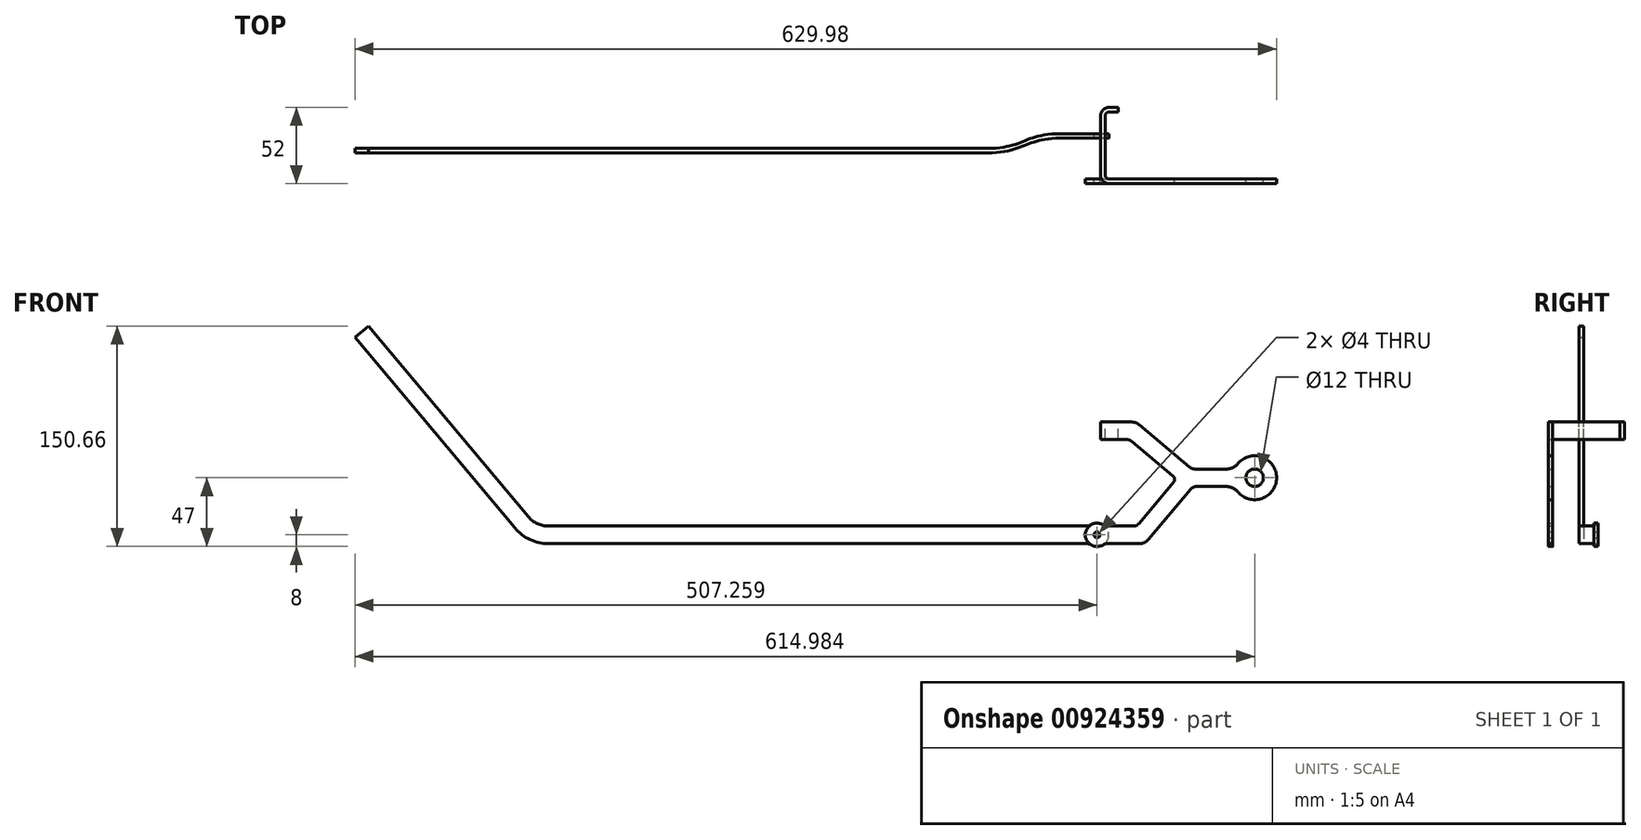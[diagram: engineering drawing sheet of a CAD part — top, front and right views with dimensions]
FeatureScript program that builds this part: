
annotation { "Feature Type Name" : "Feature", "Feature Type Description" : "" }
export const myFeature = defineFeature(function(context is Context, id is Id, definition is map)
    precondition{}
    {
        {
            var Q0;
            Q0=qCreatedBy(makeId("Front.planeOp"),FACE);
            var sketch = newSketch(context, id + "F0", { "sketchPlane" : qUnion([Q0])});
            skLineSegment(sketch, "E0", {"start": v(13.99, 0) * mm, "end": v(313.99, 0) * mm});
            skLineSegment(sketch, "E1", {"start": v(-9, 10.72) * mm, "end": v(-118.27, 140.94) * mm});
            skLineSegment(sketch, "E2", {"start": v(-23.81, 6) * mm, "end": v(-4.01, 6) * mm, "construction": true});
            skPoint(sketch, "E3.visualSharp", {"position": v(0, 0) * mm});
            skArc(sketch, "E3.filletArc", {"start": v(-9, 10.72) * mm, "mid": v(1.31, 2.81) * mm, "end": v(13.99, 0) * mm});
            skLineSegment(sketch, "E4.0", {"start": v(13.99, 12) * mm, "end": v(313.99, 12) * mm});
            skArc(sketch, "E4.1", {"start": v(0.2, 18.43) * mm, "mid": v(6.38, 13.69) * mm, "end": v(13.99, 12) * mm});
            skLineSegment(sketch, "E4.2", {"start": v(0.2, 18.43) * mm, "end": v(-109.07, 148.66) * mm});
            skLineSegment(sketch, "E5", {"start": v(-109.07, 148.66) * mm, "end": v(-118.27, 140.94) * mm});
            skLineSegment(sketch, "E6", {"start": v(313.99, 12) * mm, "end": v(313.99, 0) * mm});
            skSolve(sketch);
        }
        {
            var Q0;
            Q0=makeQuery(id+"F0.imprint","IMPRINT",FACE,{"disambiguationData":[TD([[makeQuery(id+"F0.imprint","IMPRINT",EDGE,{"derivedFrom":sQuery(id+"F0.wireOp",EDGE,"E0")}),1.0]])]});
            extrude(context, id + "F1", {"entities" : qUnion([Q0]), "depth" : 3 * mm, "offsetDistance" : 25 * mm});
        }
        {
            var Q0;
            Q0=qCreatedBy(makeId("Top.planeOp"),FACE);
            var sketch = newSketch(context, id + "F2", { "sketchPlane" : qUnion([Q0])});
            skLineSegment(sketch, "E7.0", {"start": v(13.99, 0) * mm, "end": v(313.99, 0) * mm});
            skSolve(sketch);
        }
        {
            var Q0;
            Q0=makeQuery(id+"F1.opExtrude","CAP_FACE",FACE,{"disambiguationData":[OSD([sQuery(id+"F0.wireOp",EDGE,"E0"),sQuery(id+"F0.wireOp",EDGE,"E1"),sQuery(id+"F0.wireOp",EDGE,"E3.filletArc"),sQuery(id+"F0.wireOp",EDGE,"E4.0"),sQuery(id+"F0.wireOp",EDGE,"E4.1"),sQuery(id+"F0.wireOp",EDGE,"E4.2"),sQuery(id+"F0.wireOp",EDGE,"E5"),sQuery(id+"F0.wireOp",EDGE,"E6")])],"isStart":true});
            cPlane(context, id + "F3", {"entities" : qUnion([Q0]), "cplaneType" : CPlaneType.OFFSET, "offset" : 25 * mm, "width" : 150 * mm, "height" : 150 * mm});
        }
        {
            var Q0;
            Q0=makeQuery(id+"F1.opExtrude","SWEPT_FACE",FACE,{"disambiguationData":[OSD([sQuery(id+"F0.wireOp",EDGE,"E0")])]});
            var sketch = newSketch(context, id + "F4", { "sketchPlane" : qUnion([Q0])});
            skPoint(sketch, "E8.0", {"position": v(313.99, 0) * mm});
            skFitSpline(sketch, "E9", {"points": [v(313.99, 0) * mm, v(363.99, -10) * mm], "startDerivative": vector(75, 0) * mm, "endDerivative": vector(75, 0) * mm});
            skLineSegment(sketch, "E10", {"start": v(363.99, -10) * mm, "end": v(388.99, -10) * mm});
            skLineSegment(sketch, "E11", {"start": v(363.99, -10) * mm, "end": v(241.15, -10) * mm, "construction": true});
            skSolve(sketch);
        }
        {
            var Q0;
            Q0=makeQuery(id+"F1.opExtrude","SWEPT_FACE",FACE,{"disambiguationData":[OSD([sQuery(id+"F0.wireOp",EDGE,"E6")])]});
            var Q1;
            Q1=sQuery(id+"F4.wireOp",EDGE,"E9");
            var Q2;
            Q2=sQuery(id+"F4.wireOp",EDGE,"E10");
            sweep(context, id + "F5", {"operationType" : NewBodyOperationType.ADD, "profiles" : qUnion([Q0]), "path" : qUnion([Q1, Q2])});
        }
        {
            var Q0;
            {var subQ0=sQuery(id+"F4.wireOp",EDGE,"E10");var subQ1=sQuery(id+"F0.wireOp",EDGE,"E6");Q0=makeQuery(id+"F5.opSweep","SWEPT_FACE",FACE,{"disambiguationData":[OSD([subQ1,subQ0]),TDD([makeQuery(id+"F1.opExtrude","CAP_EDGE",EDGE,{"disambiguationData":[OSD([subQ1])],"isStart":true}),subQ0])]});}
            var sketch = newSketch(context, id + "F6", { "sketchPlane" : qUnion([Q0])});
            skCircle(sketch, "E12", {"center": v(-388.99, 6) * mm, "radius": 6 * mm});
            skCircle(sketch, "E13", {"center": v(-388.99, 6) * mm, "radius": 2 * mm});
            skCircle(sketch, "E14", {"center": v(-388.99, 6) * mm, "radius": 8 * mm});
            skSolve(sketch);
        }
        {
            var Q0;
            {var subQ2=sQuery(id+"F0.wireOp",EDGE,"E6");var subQ4=sQuery(id+"F4.wireOp",EDGE,"E10");var subQ5=sQuery(id+"F0.wireOp",EDGE,"E0");var subQ6=makeQuery(id+"F5.opSweep","SWEPT_EDGE",EDGE,{"disambiguationData":[OSD([subQ5,subQ2,subQ4]),TDD([makeQuery(id+"F1.opExtrude","CAP_VERTEX",VERTEX,{"disambiguationData":[OSD([subQ5,subQ2])],"isStart":true}),subQ4])]});var subQ11=sQuery(id+"F6.wireOp",EDGE,"E14");var subQ13=makeQuery(id+"F6.imprint","INTERSECT",VERTEX,{"derivedFrom":[subQ6,subQ11]});Q0=makeQuery(id+"F6.imprint","IMPRINT",FACE,{"disambiguationData":[TD([[makeQuery(id+"F6.imprint","IMPRINT",EDGE,{"disambiguationData":[TD([[subQ13,1.0]])],"derivedFrom":subQ11}),1.0]])]});}
            var Q1;
            {var subQ1=sQuery(id+"F4.wireOp",VERTEX,"E10.end");var subQ2=sQuery(id+"F0.wireOp",EDGE,"E6");var subQ3=makeQuery(id+"F5.opSweep","CAP_EDGE",EDGE,{"disambiguationData":[OSD([subQ2,subQ1]),TDD([makeQuery(id+"F1.opExtrude","CAP_EDGE",EDGE,{"disambiguationData":[OSD([subQ2])],"isStart":true}),subQ1])],"isStart":false});var subQ9=sQuery(id+"F6.wireOp",EDGE,"E13");var subQ10=makeQuery(id+"F6.imprint","INTERSECT",VERTEX,{"disambiguationData":[OD(0.0)],"derivedFrom":[subQ3,subQ9]});Q1=makeQuery(id+"F6.imprint","IMPRINT",FACE,{"disambiguationData":[TD([[makeQuery(id+"F6.imprint","IMPRINT",EDGE,{"disambiguationData":[TD([[subQ10,1.0]])],"derivedFrom":subQ9}),-1.0]])]});}
            var Q2;
            {var subQ1=sQuery(id+"F4.wireOp",VERTEX,"E10.end");var subQ2=sQuery(id+"F0.wireOp",EDGE,"E6");var subQ3=makeQuery(id+"F5.opSweep","CAP_EDGE",EDGE,{"disambiguationData":[OSD([subQ2,subQ1]),TDD([makeQuery(id+"F1.opExtrude","CAP_EDGE",EDGE,{"disambiguationData":[OSD([subQ2])],"isStart":true}),subQ1])],"isStart":false});var subQ9=sQuery(id+"F6.wireOp",EDGE,"E13");var subQ10=makeQuery(id+"F6.imprint","INTERSECT",VERTEX,{"disambiguationData":[OD(0.0)],"derivedFrom":[subQ3,subQ9]});Q2=makeQuery(id+"F6.imprint","IMPRINT",FACE,{"disambiguationData":[TD([[makeQuery(id+"F6.imprint","IMPRINT",EDGE,{"disambiguationData":[TD([[subQ10,-1.0]])],"derivedFrom":subQ9}),-1.0]])]});}
            var Q3;
            {var subQ2=sQuery(id+"F0.wireOp",EDGE,"E6");var subQ4=sQuery(id+"F4.wireOp",EDGE,"E10");var subQ5=sQuery(id+"F0.wireOp",EDGE,"E0");var subQ6=makeQuery(id+"F5.opSweep","SWEPT_EDGE",EDGE,{"disambiguationData":[OSD([subQ5,subQ2,subQ4]),TDD([makeQuery(id+"F1.opExtrude","CAP_VERTEX",VERTEX,{"disambiguationData":[OSD([subQ5,subQ2])],"isStart":true}),subQ4])]});var subQ11=sQuery(id+"F6.wireOp",EDGE,"E14");var subQ12=makeQuery(id+"F6.imprint","INTERSECT",VERTEX,{"derivedFrom":[subQ6,subQ11]});Q3=makeQuery(id+"F6.imprint","IMPRINT",FACE,{"disambiguationData":[TD([[makeQuery(id+"F6.imprint","IMPRINT",EDGE,{"disambiguationData":[TD([[subQ12,-1.0]])],"derivedFrom":subQ11}),1.0]])]});}
            var Q4;
            {var subQ0=sQuery(id+"F6.wireOp",EDGE,"E13");var subQ1=sQuery(id+"F4.wireOp",VERTEX,"E10.end");var subQ2=sQuery(id+"F0.wireOp",EDGE,"E6");var subQ3=makeQuery(id+"F5.opSweep","CAP_EDGE",EDGE,{"disambiguationData":[OSD([subQ2,subQ1]),TDD([makeQuery(id+"F1.opExtrude","CAP_EDGE",EDGE,{"disambiguationData":[OSD([subQ2])],"isStart":true}),subQ1])],"isStart":false});var subQ4=makeQuery(id+"F6.imprint","INTERSECT",VERTEX,{"disambiguationData":[OD(0.0)],"derivedFrom":[subQ3,subQ0]});Q4=makeQuery(id+"F6.imprint","IMPRINT",FACE,{"disambiguationData":[TD([[makeQuery(id+"F6.imprint","IMPRINT",EDGE,{"disambiguationData":[TD([[subQ4,1.0]])],"derivedFrom":subQ0}),1.0]])]});}
            var Q5;
            {var subQ0=sQuery(id+"F6.wireOp",EDGE,"E13");var subQ1=sQuery(id+"F4.wireOp",VERTEX,"E10.end");var subQ2=sQuery(id+"F0.wireOp",EDGE,"E6");var subQ3=makeQuery(id+"F5.opSweep","CAP_EDGE",EDGE,{"disambiguationData":[OSD([subQ2,subQ1]),TDD([makeQuery(id+"F1.opExtrude","CAP_EDGE",EDGE,{"disambiguationData":[OSD([subQ2])],"isStart":true}),subQ1])],"isStart":false});var subQ4=makeQuery(id+"F6.imprint","INTERSECT",VERTEX,{"disambiguationData":[OD(0.0)],"derivedFrom":[subQ3,subQ0]});Q5=makeQuery(id+"F6.imprint","IMPRINT",FACE,{"disambiguationData":[TD([[makeQuery(id+"F6.imprint","IMPRINT",EDGE,{"disambiguationData":[TD([[subQ4,-1.0]])],"derivedFrom":subQ0}),1.0]])]});}
            extrude(context, id + "F7", {"entities" : qUnion([Q0, Q1, Q2, Q3, Q4, Q5]), "operationType" : NewBodyOperationType.ADD, "oppositeDirection" : true, "depth" : 3 * mm, "offsetDistance" : 25 * mm});
        }
        {
            var Q0;
            {var subQ0=sQuery(id+"F6.wireOp",EDGE,"E13");var subQ1=sQuery(id+"F4.wireOp",VERTEX,"E10.end");var subQ2=sQuery(id+"F0.wireOp",EDGE,"E6");var subQ3=makeQuery(id+"F5.opSweep","CAP_EDGE",EDGE,{"disambiguationData":[OSD([subQ2,subQ1]),TDD([makeQuery(id+"F1.opExtrude","CAP_EDGE",EDGE,{"disambiguationData":[OSD([subQ2])],"isStart":true}),subQ1])],"isStart":false});var subQ4=makeQuery(id+"F6.imprint","INTERSECT",VERTEX,{"disambiguationData":[OD(0.0)],"derivedFrom":[subQ3,subQ0]});Q0=makeQuery(id+"F6.imprint","IMPRINT",FACE,{"disambiguationData":[TD([[makeQuery(id+"F6.imprint","IMPRINT",EDGE,{"disambiguationData":[TD([[subQ4,1.0]])],"derivedFrom":subQ0}),1.0]])]});}
            var Q1;
            {var subQ0=sQuery(id+"F6.wireOp",EDGE,"E13");var subQ1=sQuery(id+"F4.wireOp",VERTEX,"E10.end");var subQ2=sQuery(id+"F0.wireOp",EDGE,"E6");var subQ3=makeQuery(id+"F5.opSweep","CAP_EDGE",EDGE,{"disambiguationData":[OSD([subQ2,subQ1]),TDD([makeQuery(id+"F1.opExtrude","CAP_EDGE",EDGE,{"disambiguationData":[OSD([subQ2])],"isStart":true}),subQ1])],"isStart":false});var subQ4=makeQuery(id+"F6.imprint","INTERSECT",VERTEX,{"disambiguationData":[OD(0.0)],"derivedFrom":[subQ3,subQ0]});Q1=makeQuery(id+"F6.imprint","IMPRINT",FACE,{"disambiguationData":[TD([[makeQuery(id+"F6.imprint","IMPRINT",EDGE,{"disambiguationData":[TD([[subQ4,-1.0]])],"derivedFrom":subQ0}),1.0]])]});}
            extrude(context, id + "F8", {"entities" : qUnion([Q0, Q1]), "operationType" : NewBodyOperationType.REMOVE, "oppositeDirection" : true, "depth" : 25 * mm, "offsetDistance" : 25 * mm});
        }
        {
            var Q0;
            {var subQ0=sQuery(id+"F0.wireOp",EDGE,"E4.0");Q0=makeQuery(id+"F7.boolean.opBoolean","INTERSECT",EDGE,{"derivedFrom":[makeQuery(id+"F5.boolean.opBoolean","MERGE",FACE,{"derivedFrom":[makeQuery(id+"F1.opExtrude","SWEPT_FACE",FACE,{"disambiguationData":[OSD([subQ0])]}),makeQuery(id+"F5.opSweep","SWEPT_FACE",FACE,{"disambiguationData":[OSD([subQ0,sQuery(id+"F0.wireOp",EDGE,"E6"),sQuery(id+"F4.wireOp",EDGE,"E9")])]})]}),makeQuery(id+"F7.opExtrude","SWEPT_FACE",FACE,{"disambiguationData":[OSD([sQuery(id+"F6.wireOp",EDGE,"E14")])]})]});}
            var Q1;
            {var subQ0=sQuery(id+"F0.wireOp",EDGE,"E0");Q1=makeQuery(id+"F7.boolean.opBoolean","INTERSECT",EDGE,{"derivedFrom":[makeQuery(id+"F5.boolean.opBoolean","MERGE",FACE,{"derivedFrom":[makeQuery(id+"F1.opExtrude","SWEPT_FACE",FACE,{"disambiguationData":[OSD([subQ0])]}),makeQuery(id+"F5.opSweep","SWEPT_FACE",FACE,{"disambiguationData":[OSD([subQ0,sQuery(id+"F0.wireOp",EDGE,"E6"),sQuery(id+"F4.wireOp",EDGE,"E9")])]})]}),makeQuery(id+"F7.opExtrude","SWEPT_FACE",FACE,{"disambiguationData":[OSD([sQuery(id+"F6.wireOp",EDGE,"E14")])]})]});}
            fillet(context, id + "F9", {"entities" : qUnion([Q0, Q1]), "radius" : 5 * mm, "tangentPropagation" : true, "allowEdgeOverflow" : false});
        }
        {
            var Q0;
            Q0=qCreatedBy(id+"F3.planeOp",FACE);
            var sketch = newSketch(context, id + "F10", { "sketchPlane" : qUnion([Q0])});
            skArc(sketch, "E15.0", {"start": v(-393.25, -0.77) * mm, "mid": v(-380.99, 6) * mm, "end": v(-393.25, 12.77) * mm});
            skPoint(sketch, "E16.orphan", {"position": v(-382.06, 12) * mm});
            skPoint(sketch, "E17.orphan", {"position": v(-388.99, 0) * mm});
            skPoint(sketch, "E18.orphan", {"position": v(-363.99, 12) * mm});
            skPoint(sketch, "E19.orphan", {"position": v(-363.99, 0) * mm});
            skLineSegment(sketch, "E20", {"start": v(-363.99, 0) * mm, "end": v(-363.99, -55) * mm, "construction": true});
            skLineSegment(sketch, "E21", {"start": v(-363.99, -55) * mm, "end": v(-590.7, -55) * mm, "construction": true});
            skCircle(sketch, "E22", {"center": v(-496.71, 45) * mm, "radius": 100 * mm});
            skArc(sketch, "E23", {"start": v(-485.19, 54.6) * mm, "mid": v(-511.71, 45) * mm, "end": v(-485.19, 35.4) * mm});
            skLineSegment(sketch, "E24", {"start": v(-388.99, 6) * mm, "end": v(-418.99, 6) * mm, "construction": true});
            skLineSegment(sketch, "E25", {"start": v(-418.99, 6) * mm, "end": v(-451.71, 45) * mm, "construction": true});
            skLineSegment(sketch, "E26", {"start": v(-451.71, 45) * mm, "end": v(-481.71, 45) * mm, "construction": true});
            skLineSegment(sketch, "E27.0", {"start": v(-455.72, 51) * mm, "end": v(-477.5, 51) * mm});
            skLineSegment(sketch, "E27.1", {"start": v(-417.7, 13.79) * mm, "end": v(-441.33, 41.96) * mm});
            skLineSegment(sketch, "E27.2", {"start": v(-395.92, 12) * mm, "end": v(-413.86, 12) * mm});
            skLineSegment(sketch, "E28.0", {"start": v(-456.84, 39) * mm, "end": v(-477.5, 39) * mm});
            skLineSegment(sketch, "E28.1", {"start": v(-424.18, 2.86) * mm, "end": v(-453.01, 37.21) * mm});
            skLineSegment(sketch, "E28.2", {"start": v(-395.92, 0) * mm, "end": v(-418.06, 0) * mm});
            skPoint(sketch, "E29.visualSharp", {"position": v(-482.97, 51) * mm});
            skArc(sketch, "E29.filletArc", {"start": v(-485.19, 54.6) * mm, "mid": v(-481.75, 51.94) * mm, "end": v(-477.5, 51) * mm});
            skPoint(sketch, "E30.visualSharp", {"position": v(-482.97, 39) * mm});
            skArc(sketch, "E30.filletArc", {"start": v(-477.5, 39) * mm, "mid": v(-481.75, 38.06) * mm, "end": v(-485.19, 35.4) * mm});
            skPoint(sketch, "E31.visualSharp", {"position": v(-454.51, 39) * mm});
            skArc(sketch, "E31.filletArc", {"start": v(-453.01, 37.21) * mm, "mid": v(-454.73, 38.53) * mm, "end": v(-456.84, 39) * mm});
            skPoint(sketch, "E32.visualSharp", {"position": v(-448.92, 51) * mm});
            skPoint(sketch, "E33.visualSharp", {"position": v(-416.2, 12) * mm});
            skArc(sketch, "E33.filletArc", {"start": v(-417.7, 13.79) * mm, "mid": v(-415.97, 12.47) * mm, "end": v(-413.86, 12) * mm});
            skPoint(sketch, "E34.visualSharp", {"position": v(-421.79, 0) * mm});
            skArc(sketch, "E34.filletArc", {"start": v(-424.18, 2.86) * mm, "mid": v(-421.44, 0.75) * mm, "end": v(-418.06, 0) * mm});
            skPoint(sketch, "E35.visualSharp", {"position": v(-394.28, 12) * mm});
            skArc(sketch, "E35.filletArc", {"start": v(-395.92, 12) * mm, "mid": v(-394.53, 12.2) * mm, "end": v(-393.25, 12.77) * mm});
            skPoint(sketch, "E36.visualSharp", {"position": v(-394.28, 0) * mm});
            skArc(sketch, "E36.filletArc", {"start": v(-393.25, -0.77) * mm, "mid": v(-394.53, -0.2) * mm, "end": v(-395.92, 0) * mm});
            skCircle(sketch, "E37", {"center": v(-496.71, 45) * mm, "radius": 6 * mm});
            skCircle(sketch, "E38.0", {"center": v(-388.99, 6) * mm, "radius": 2 * mm});
            skLineSegment(sketch, "E39", {"start": v(-451.71, 45) * mm, "end": v(-413.45, 77.1) * mm, "construction": true});
            skLineSegment(sketch, "E40.0", {"start": v(-452.5, 52.17) * mm, "end": v(-417.87, 81.23) * mm});
            skLineSegment(sketch, "E41.0", {"start": v(-440.96, 46.19) * mm, "end": v(-412.66, 69.94) * mm});
            skPoint(sketch, "E42.visualSharp", {"position": v(-453.9, 51) * mm});
            skArc(sketch, "E42.filletArc", {"start": v(-455.72, 51) * mm, "mid": v(-454, 51.3) * mm, "end": v(-452.5, 52.17) * mm});
            skPoint(sketch, "E43.visualSharp", {"position": v(-443.26, 44.26) * mm});
            skArc(sketch, "E43.filletArc", {"start": v(-440.96, 46.19) * mm, "mid": v(-442.02, 44.15) * mm, "end": v(-441.33, 41.96) * mm});
            skLineSegment(sketch, "E44", {"start": v(-413.45, 77.1) * mm, "end": v(-403.45, 77.1) * mm, "construction": true});
            skLineSegment(sketch, "E45.0", {"start": v(-409.45, 71.1) * mm, "end": v(-403.45, 71.1) * mm});
            skLineSegment(sketch, "E46.0", {"start": v(-412.72, 83.1) * mm, "end": v(-403.45, 83.1) * mm});
            skLineSegment(sketch, "E47", {"start": v(-403.45, 71.1) * mm, "end": v(-403.45, 83.1) * mm});
            skPoint(sketch, "E48.visualSharp", {"position": v(-415.64, 83.1) * mm});
            skArc(sketch, "E48.filletArc", {"start": v(-412.72, 83.1) * mm, "mid": v(-415.46, 82.62) * mm, "end": v(-417.87, 81.23) * mm});
            skPoint(sketch, "E49.visualSharp", {"position": v(-411.27, 71.1) * mm});
            skArc(sketch, "E49.filletArc", {"start": v(-409.45, 71.1) * mm, "mid": v(-411.16, 70.8) * mm, "end": v(-412.66, 69.94) * mm});
            skSolve(sketch);
        }
        {
            var Q0;
            Q0=makeQuery(id+"F10.imprint","IMPRINT",FACE,{"disambiguationData":[TD([[makeQuery(id+"F10.imprint","IMPRINT",EDGE,{"derivedFrom":sQuery(id+"F10.wireOp",EDGE,"E23")}),1.0]])]});
            var Q1;
            Q1=makeQuery(id+"F10.imprint","IMPRINT",FACE,{"disambiguationData":[TD([[makeQuery(id+"F10.imprint","IMPRINT",EDGE,{"derivedFrom":sQuery(id+"F10.wireOp",EDGE,"E15.0")}),1.0]])]});
            var Q2;
            {var subQ5=sQuery(id+"F10.wireOp",EDGE,"E47");Q2=makeQuery(id+"F10.imprint","IMPRINT",FACE,{"disambiguationData":[TD([[makeQuery(id+"F10.imprint","IMPRINT",EDGE,{"derivedFrom":subQ5}),1.0]])]});}
            extrude(context, id + "F11", {"entities" : qUnion([Q0, Q1, Q2]), "depth" : 3 * mm, "offsetDistance" : 25 * mm});
        }
        {
            var Q0;
            Q0=makeQuery(id+"F11.opExtrude","SWEPT_FACE",FACE,{"disambiguationData":[OSD([sQuery(id+"F10.wireOp",EDGE,"E46.0")])]});
            var sketch = newSketch(context, id + "F12", { "sketchPlane" : qUnion([Q0])});
            skLineSegment(sketch, "E50.0", {"start": v(412.72, 25) * mm, "end": v(403.45, 25) * mm});
            skLineSegment(sketch, "E51", {"start": v(403.45, 25) * mm, "end": v(397.45, 25) * mm});
            skLineSegment(sketch, "E52", {"start": v(394.45, 22) * mm, "end": v(394.45, -18) * mm});
            skPoint(sketch, "E53.visualSharp", {"position": v(394.45, 25) * mm});
            skArc(sketch, "E53.filletArc", {"start": v(397.45, 25) * mm, "mid": v(395.33, 24.12) * mm, "end": v(394.45, 22) * mm});
            skLineSegment(sketch, "E54", {"start": v(394.45, 2) * mm, "end": v(428.98, 2) * mm, "construction": true});
            skLineSegment(sketch, "E55.MirrorCS", {"start": v(403.45, -21) * mm, "end": v(397.45, -21) * mm});
            skArc(sketch, "E56.MirrorCS", {"start": v(397.45, -21) * mm, "mid": v(395.33, -20.12) * mm, "end": v(394.45, -18) * mm});
            skSolve(sketch);
        }
        {
            var Q0;
            Q0=makeQuery(id+"F11.opExtrude","SWEPT_FACE",FACE,{"disambiguationData":[OSD([sQuery(id+"F10.wireOp",EDGE,"E47")])]});
            var sketch = newSketch(context, id + "F13", { "sketchPlane" : qUnion([Q0])});
            skLineSegment(sketch, "E57.0.0", {"start": v(-25, 71.1) * mm, "end": v(-25, 83.1) * mm});
            skLineSegment(sketch, "E57.0.1", {"start": v(-25, 83.1) * mm, "end": v(-28, 83.1) * mm});
            skLineSegment(sketch, "E57.0.2", {"start": v(-28, 83.1) * mm, "end": v(-28, 71.1) * mm});
            skLineSegment(sketch, "E57.0.3", {"start": v(-28, 71.1) * mm, "end": v(-25, 71.1) * mm});
            skSolve(sketch);
        }
        {
            var Q0;
            Q0=makeQuery(id+"F13.imprint","IMPRINT",FACE,{"disambiguationData":[TD([[makeQuery(id+"F13.imprint","IMPRINT",EDGE,{"derivedFrom":sQuery(id+"F13.wireOp",EDGE,"E57.0.0")}),1.0]])]});
            var Q1;
            Q1=sQuery(id+"F12.wireOp",EDGE,"E51");
            var Q2;
            Q2=sQuery(id+"F12.wireOp",EDGE,"E53.filletArc");
            var Q3;
            Q3=sQuery(id+"F12.wireOp",EDGE,"E52");
            var Q4;
            Q4=sQuery(id+"F12.wireOp",EDGE,"E56.MirrorCS");
            var Q5;
            Q5=sQuery(id+"F12.wireOp",EDGE,"E55.MirrorCS");
            sweep(context, id + "F14", {"operationType" : NewBodyOperationType.ADD, "profiles" : qUnion([Q0]), "path" : qUnion([Q1, Q2, Q3, Q4, Q5])});
        }
        {
            var Q0;
            Q0=sQuery(id+"F12.wireOp",EDGE,"E54");
            cPlane(context, id + "F15", {"entities" : qUnion([Q0]), "cplaneType" : CPlaneType.LINE_ANGLE, "offset" : 25 * mm, "angle" : 0 * degree, "width" : 150 * mm, "height" : 150 * mm});
        }
        {
            var Q0;
            Q0=makeQuery(id+"F11.opExtrude","SWEPT_BODY",BODY,{"disambiguationData":[OSD([sQuery(id+"F10.wireOp",EDGE,"E15.0"),sQuery(id+"F10.wireOp",EDGE,"E23"),sQuery(id+"F10.wireOp",EDGE,"E27.0"),sQuery(id+"F10.wireOp",EDGE,"E27.1"),sQuery(id+"F10.wireOp",EDGE,"E27.2"),sQuery(id+"F10.wireOp",EDGE,"E28.0"),sQuery(id+"F10.wireOp",EDGE,"E28.1"),sQuery(id+"F10.wireOp",EDGE,"E28.2"),sQuery(id+"F10.wireOp",EDGE,"E29.filletArc"),sQuery(id+"F10.wireOp",EDGE,"E30.filletArc"),sQuery(id+"F10.wireOp",EDGE,"E31.filletArc"),sQuery(id+"F10.wireOp",EDGE,"E33.filletArc"),sQuery(id+"F10.wireOp",EDGE,"E34.filletArc"),sQuery(id+"F10.wireOp",EDGE,"E35.filletArc"),sQuery(id+"F10.wireOp",EDGE,"E36.filletArc"),sQuery(id+"F10.wireOp",EDGE,"E37"),sQuery(id+"F10.wireOp",EDGE,"E38.0"),sQuery(id+"F10.wireOp",EDGE,"E40.0"),sQuery(id+"F10.wireOp",EDGE,"E41.0"),sQuery(id+"F10.wireOp",EDGE,"E42.filletArc"),sQuery(id+"F10.wireOp",EDGE,"E43.filletArc"),sQuery(id+"F10.wireOp",EDGE,"E45.0"),sQuery(id+"F10.wireOp",EDGE,"E46.0"),sQuery(id+"F10.wireOp",EDGE,"E47"),sQuery(id+"F10.wireOp",EDGE,"E48.filletArc"),sQuery(id+"F10.wireOp",EDGE,"E49.filletArc")])]});
            var Q1;
            Q1=qCreatedBy(id+"F15.planeOp",FACE);
            mirror(context, id + "F16", {"operationType" : NewBodyOperationType.ADD, "entities" : qUnion([Q0]), "mirrorPlane" : qUnion([Q1])});
        }
        {
            var Q0;
            Q0=makeQuery(id+"F11.opExtrude","SWEPT_BODY",BODY,{"disambiguationData":[OSD([sQuery(id+"F10.wireOp",EDGE,"E15.0"),sQuery(id+"F10.wireOp",EDGE,"E23"),sQuery(id+"F10.wireOp",EDGE,"E27.0"),sQuery(id+"F10.wireOp",EDGE,"E27.1"),sQuery(id+"F10.wireOp",EDGE,"E27.2"),sQuery(id+"F10.wireOp",EDGE,"E28.0"),sQuery(id+"F10.wireOp",EDGE,"E28.1"),sQuery(id+"F10.wireOp",EDGE,"E28.2"),sQuery(id+"F10.wireOp",EDGE,"E29.filletArc"),sQuery(id+"F10.wireOp",EDGE,"E30.filletArc"),sQuery(id+"F10.wireOp",EDGE,"E31.filletArc"),sQuery(id+"F10.wireOp",EDGE,"E33.filletArc"),sQuery(id+"F10.wireOp",EDGE,"E34.filletArc"),sQuery(id+"F10.wireOp",EDGE,"E35.filletArc"),sQuery(id+"F10.wireOp",EDGE,"E36.filletArc"),sQuery(id+"F10.wireOp",EDGE,"E37"),sQuery(id+"F10.wireOp",EDGE,"E38.0"),sQuery(id+"F10.wireOp",EDGE,"E40.0"),sQuery(id+"F10.wireOp",EDGE,"E41.0"),sQuery(id+"F10.wireOp",EDGE,"E42.filletArc"),sQuery(id+"F10.wireOp",EDGE,"E43.filletArc"),sQuery(id+"F10.wireOp",EDGE,"E45.0"),sQuery(id+"F10.wireOp",EDGE,"E46.0"),sQuery(id+"F10.wireOp",EDGE,"E47"),sQuery(id+"F10.wireOp",EDGE,"E48.filletArc"),sQuery(id+"F10.wireOp",EDGE,"E49.filletArc")])]});
            deleteBodies(context, id + "F17", {"entities" : qUnion([Q0])});
        }
    });
